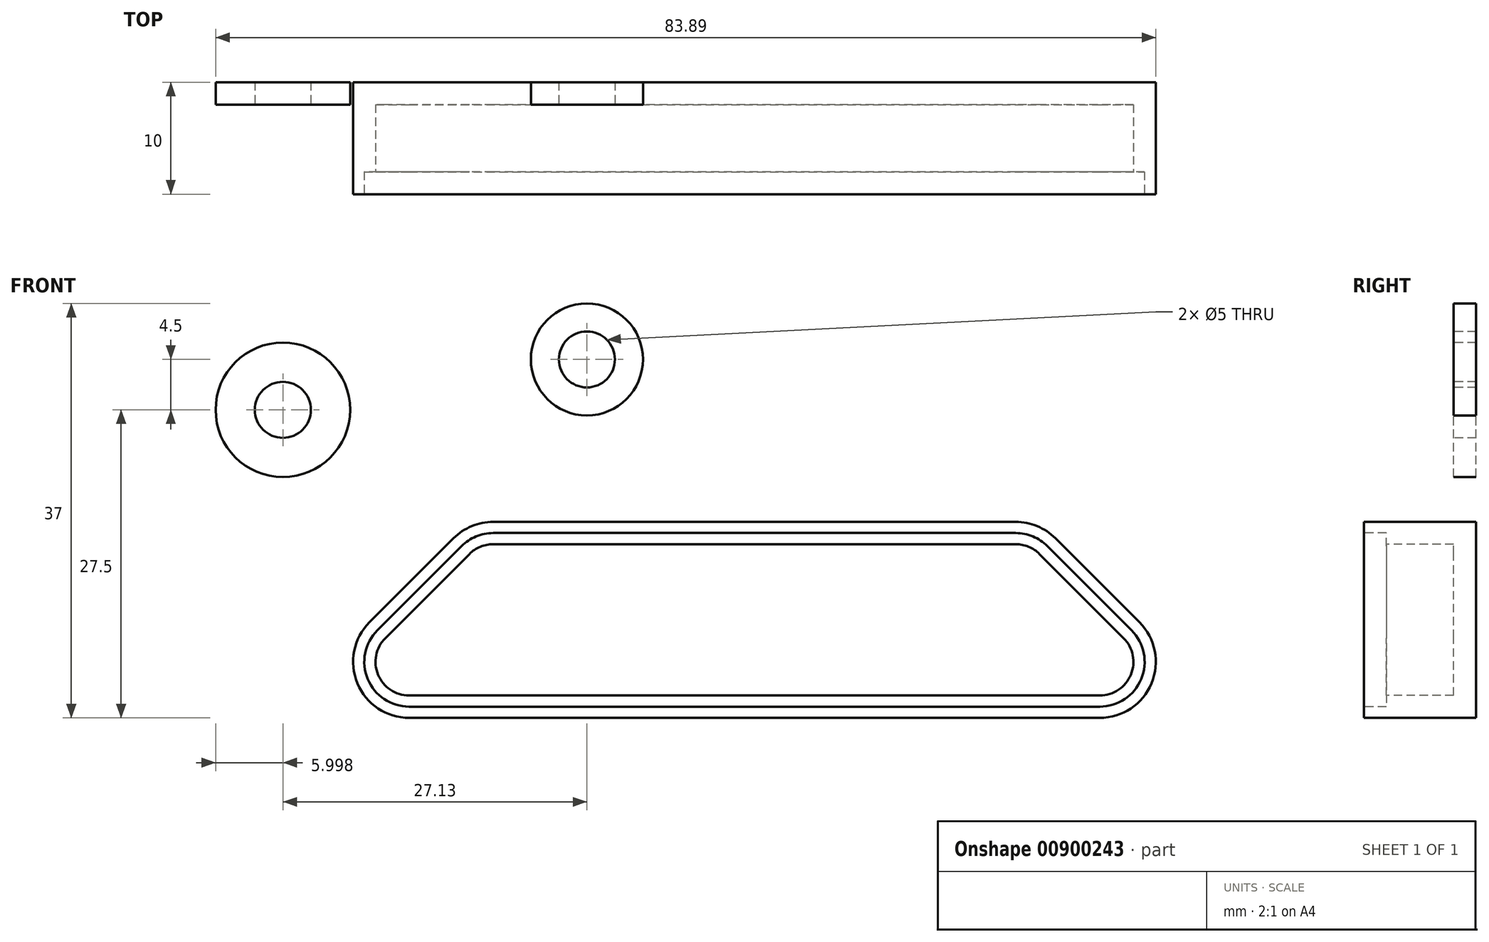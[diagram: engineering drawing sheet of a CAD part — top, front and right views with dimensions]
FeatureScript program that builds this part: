
annotation { "Feature Type Name" : "Feature", "Feature Type Description" : "" }
export const myFeature = defineFeature(function(context is Context, id is Id, definition is map)
    precondition{}
    {
        {
            var Q0;
            Q0=qCreatedBy(makeId("Front.planeOp"),FACE);
            var sketch = newSketch(context, id + "F0", { "sketchPlane" : qUnion([Q0])});
            skLineSegment(sketch, "E0", {"start": v(-37.2, 0) * mm, "end": v(34.97, 0) * mm, "construction": true});
            skArc(sketch, "E1", {"start": v(34.97, -20) * mm, "mid": v(54.97, 0) * mm, "end": v(34.97, 20) * mm});
            skArc(sketch, "E2", {"start": v(-37.2, 20) * mm, "mid": v(-57.2, 0) * mm, "end": v(-37.2, -20) * mm});
            skLineSegment(sketch, "E3", {"start": v(-37.2, 20) * mm, "end": v(34.97, 20) * mm});
            skLineSegment(sketch, "E4.MirrorCS", {"start": v(-37.2, -20) * mm, "end": v(34.97, -20) * mm});
            skSolve(sketch);
        }
        {
            var Q0;
            Q0=qSketchRegion(id+"F0",true);
            extrude(context, id + "F1", {"entities" : qUnion([Q0]), "depth" : 2 * mm, "offsetDistance" : 25 * mm});
        }
        {
            var Q0;
            Q0=makeQuery(id+"F1.opExtrude","CAP_FACE",FACE,{"disambiguationData":[OSD([sQuery(id+"F0.wireOp",EDGE,"E1"),sQuery(id+"F0.wireOp",EDGE,"E2"),sQuery(id+"F0.wireOp",EDGE,"E3"),sQuery(id+"F0.wireOp",EDGE,"E4.MirrorCS")])],"isStart":false});
            var sketch = newSketch(context, id + "F2", { "sketchPlane" : qUnion([Q0])});
            skLineSegment(sketch, "E5", {"start": v(0, 107.5) * mm, "end": v(0, -106.96) * mm, "construction": true});
            skLineSegment(sketch, "E6", {"start": v(0, -2.5) * mm, "end": v(23.31, -2.5) * mm});
            skLineSegment(sketch, "E7", {"start": v(26.85, -3.96) * mm, "end": v(34.35, -11.46) * mm});
            skLineSegment(sketch, "E8", {"start": v(30.81, -20) * mm, "end": v(0, -20) * mm});
            skArc(sketch, "E9.filletArc", {"start": v(26.85, -3.96) * mm, "mid": v(25.23, -2.88) * mm, "end": v(23.31, -2.5) * mm});
            skArc(sketch, "E10.filletArc", {"start": v(30.81, -20) * mm, "mid": v(35.43, -16.91) * mm, "end": v(34.35, -11.46) * mm});
            skLineSegment(sketch, "E11.MirrorCS", {"start": v(0, -2.5) * mm, "end": v(-23.31, -2.5) * mm});
            skArc(sketch, "E12.MirrorCS", {"start": v(-26.85, -3.96) * mm, "mid": v(-25.23, -2.88) * mm, "end": v(-23.31, -2.5) * mm});
            skLineSegment(sketch, "E13.MirrorCS", {"start": v(-26.85, -3.96) * mm, "end": v(-34.35, -11.46) * mm});
            skArc(sketch, "E14.MirrorCS", {"start": v(-30.81, -20) * mm, "mid": v(-35.43, -16.91) * mm, "end": v(-34.35, -11.46) * mm});
            skLineSegment(sketch, "E15.MirrorCS", {"start": v(-30.81, -20) * mm, "end": v(0, -20) * mm});
            skSolve(sketch);
        }
        {
            var Q0;
            Q0=makeQuery(id+"F2.imprint","IMPRINT",FACE,{"disambiguationData":[TD([[makeQuery(id+"F2.imprint","IMPRINT",EDGE,{"derivedFrom":sQuery(id+"F2.wireOp",EDGE,"E6")}),-1.0]])]});
            var Q1;
            Q1=makeQuery(id+"F2.imprint","IMPRINT",FACE,{"disambiguationData":[TD([[makeQuery(id+"F2.imprint","IMPRINT",EDGE,{"derivedFrom":sQuery(id+"F2.wireOp",EDGE,"1ff64fa8-2fd5-4123-b6a7-406101e30ad4.0")}),1.0]])]});
            var Q2;
            Q2=makeQuery(id+"F2.imprint","IMPRINT",FACE,{"disambiguationData":[TD([[makeQuery(id+"F2.imprint","IMPRINT",EDGE,{"derivedFrom":sQuery(id+"F2.wireOp",EDGE,"6d2cac0a-8418-49f5-aced-8188614ca164.0")}),1.0]])]});
            extrude(context, id + "F3", {"entities" : qUnion([Q0, Q1, Q2]), "operationType" : NewBodyOperationType.ADD, "depth" : 8 * mm, "offsetDistance" : 25 * mm});
        }
        {
            var Q0;
            Q0=makeQuery(id+"F3.opExtrude","CAP_FACE",FACE,{"disambiguationData":[OSD([sQuery(id+"F2.wireOp",EDGE,"E6"),sQuery(id+"F2.wireOp",EDGE,"E7"),sQuery(id+"F2.wireOp",EDGE,"E8"),sQuery(id+"F2.wireOp",EDGE,"E9.filletArc"),sQuery(id+"F2.wireOp",EDGE,"E10.filletArc"),sQuery(id+"F2.wireOp",EDGE,"E11.MirrorCS"),sQuery(id+"F2.wireOp",EDGE,"E12.MirrorCS"),sQuery(id+"F2.wireOp",EDGE,"E13.MirrorCS"),sQuery(id+"F2.wireOp",EDGE,"E14.MirrorCS"),sQuery(id+"F2.wireOp",EDGE,"E15.MirrorCS")])],"isStart":false});
            var sketch = newSketch(context, id + "F4", { "sketchPlane" : qUnion([Q0])});
            skArc(sketch, "E16.0", {"start": v(-33.64, -12.17) * mm, "mid": v(-34.51, -16.53) * mm, "end": v(-30.81, -19) * mm});
            skLineSegment(sketch, "E16.1", {"start": v(-26.14, -4.67) * mm, "end": v(-33.64, -12.17) * mm});
            skLineSegment(sketch, "E16.2", {"start": v(-30.81, -19) * mm, "end": v(30.81, -19) * mm});
            skArc(sketch, "E16.3", {"start": v(-23.31, -3.5) * mm, "mid": v(-24.85, -3.8) * mm, "end": v(-26.14, -4.67) * mm});
            skArc(sketch, "E16.4", {"start": v(30.81, -19) * mm, "mid": v(34.51, -16.53) * mm, "end": v(33.64, -12.17) * mm});
            skLineSegment(sketch, "E16.5", {"start": v(33.64, -12.17) * mm, "end": v(26.14, -4.67) * mm});
            skArc(sketch, "E16.6", {"start": v(26.14, -4.67) * mm, "mid": v(24.85, -3.8) * mm, "end": v(23.31, -3.5) * mm});
            skLineSegment(sketch, "E16.7", {"start": v(23.31, -3.5) * mm, "end": v(-23.31, -3.5) * mm});
            skSolve(sketch);
        }
        {
            var Q0;
            Q0=makeQuery(id+"F4.imprint","IMPRINT",FACE,{"disambiguationData":[TD([[makeQuery(id+"F4.imprint","IMPRINT",EDGE,{"derivedFrom":sQuery(id+"F4.wireOp",EDGE,"E16.0")}),1.0]])]});
            extrude(context, id + "F5", {"entities" : qUnion([Q0]), "operationType" : NewBodyOperationType.REMOVE, "oppositeDirection" : true, "depth" : 2 * mm, "offsetDistance" : 25 * mm});
        }
        {
            var Q0;
            Q0=makeQuery(id+"F5.boolean.opBoolean","COPY",FACE,{"derivedFrom":makeQuery(id+"F5.opExtrude","CAP_FACE",FACE,{"disambiguationData":[OSD([sQuery(id+"F4.wireOp",EDGE,"E16.0"),sQuery(id+"F4.wireOp",EDGE,"E16.1"),sQuery(id+"F4.wireOp",EDGE,"E16.2"),sQuery(id+"F4.wireOp",EDGE,"E16.3"),sQuery(id+"F4.wireOp",EDGE,"E16.4"),sQuery(id+"F4.wireOp",EDGE,"E16.5"),sQuery(id+"F4.wireOp",EDGE,"E16.6"),sQuery(id+"F4.wireOp",EDGE,"E16.7")])],"isStart":false})});
            var sketch = newSketch(context, id + "F6", { "sketchPlane" : qUnion([Q0])});
            skLineSegment(sketch, "E17.0", {"start": v(32.94, -12.88) * mm, "end": v(25.44, -5.38) * mm});
            skArc(sketch, "E17.1", {"start": v(30.81, -18) * mm, "mid": v(33.59, -16.15) * mm, "end": v(32.94, -12.88) * mm});
            skArc(sketch, "E17.2", {"start": v(25.44, -5.38) * mm, "mid": v(24.46, -4.73) * mm, "end": v(23.31, -4.5) * mm});
            skLineSegment(sketch, "E17.3", {"start": v(-30.81, -18) * mm, "end": v(30.81, -18) * mm});
            skLineSegment(sketch, "E17.4", {"start": v(23.31, -4.5) * mm, "end": v(-23.31, -4.5) * mm});
            skArc(sketch, "E17.5", {"start": v(-23.31, -4.5) * mm, "mid": v(-24.46, -4.73) * mm, "end": v(-25.44, -5.38) * mm});
            skLineSegment(sketch, "E17.6", {"start": v(-25.44, -5.38) * mm, "end": v(-32.94, -12.88) * mm});
            skArc(sketch, "E17.7", {"start": v(-32.94, -12.88) * mm, "mid": v(-33.59, -16.15) * mm, "end": v(-30.81, -18) * mm});
            skSolve(sketch);
        }
        {
            var Q0;
            Q0=makeQuery(id+"F6.imprint","IMPRINT",FACE,{"disambiguationData":[TD([[makeQuery(id+"F6.imprint","IMPRINT",EDGE,{"derivedFrom":sQuery(id+"F6.wireOp",EDGE,"E17.0")}),1.0]])]});
            extrude(context, id + "F7", {"entities" : qUnion([Q0]), "operationType" : NewBodyOperationType.REMOVE, "oppositeDirection" : true, "depth" : 6 * mm, "offsetDistance" : 25 * mm});
        }
        {
            var Q0;
            Q0=makeQuery(id+"F1.opExtrude","CAP_FACE",FACE,{"disambiguationData":[OSD([sQuery(id+"F0.wireOp",EDGE,"E1"),sQuery(id+"F0.wireOp",EDGE,"E2"),sQuery(id+"F0.wireOp",EDGE,"E3"),sQuery(id+"F0.wireOp",EDGE,"E4.MirrorCS")])],"isStart":false});
            var sketch = newSketch(context, id + "F8", { "sketchPlane" : qUnion([Q0])});
            skCircle(sketch, "E18", {"center": v(42.08, 7.5) * mm, "radius": 6 * mm});
            skLineSegment(sketch, "E19", {"start": v(61.14, 0) * mm, "end": v(-61.86, 0) * mm, "construction": true});
            skLineSegment(sketch, "E20", {"start": v(0, 29.23) * mm, "end": v(0, -29.55) * mm, "construction": true});
            skCircle(sketch, "E21", {"center": v(14.95, 12) * mm, "radius": 5 * mm});
            skCircle(sketch, "E22.MirrorC", {"center": v(-42.08, 7.5) * mm, "radius": 6 * mm});
            skCircle(sketch, "E23.MirrorC", {"center": v(-14.95, 12) * mm, "radius": 5 * mm});
            skSolve(sketch);
        }
        {
            var Q0;
            Q0=makeQuery(id+"F8.imprint","IMPRINT",FACE,{"disambiguationData":[TD([[makeQuery(id+"F8.imprint","IMPRINT",EDGE,{"derivedFrom":sQuery(id+"F8.wireOp",EDGE,"E23.MirrorC")}),-1.0]])]});
            var Q1;
            Q1=makeQuery(id+"F8.imprint","IMPRINT",FACE,{"disambiguationData":[TD([[makeQuery(id+"F8.imprint","IMPRINT",EDGE,{"derivedFrom":sQuery(id+"F8.wireOp",EDGE,"E22.MirrorC")}),-1.0]])]});
            var Q2;
            Q2=makeQuery(id+"F8.imprint","IMPRINT",FACE,{"disambiguationData":[TD([[makeQuery(id+"F8.imprint","IMPRINT",EDGE,{"derivedFrom":sQuery(id+"F8.wireOp",EDGE,"E21")}),1.0]])]});
            var Q3;
            Q3=makeQuery(id+"F8.imprint","IMPRINT",FACE,{"disambiguationData":[TD([[makeQuery(id+"F8.imprint","IMPRINT",EDGE,{"derivedFrom":sQuery(id+"F8.wireOp",EDGE,"E18")}),1.0]])]});
            extrude(context, id + "F9", {"entities" : qUnion([Q0, Q1, Q2, Q3]), "operationType" : NewBodyOperationType.ADD, "depth" : 1 * mm, "offsetDistance" : 25 * mm});
        }
        {
            var Q0;
            Q0=makeQuery(id+"F9.opExtrude","CAP_FACE",FACE,{"disambiguationData":[OSD([sQuery(id+"F8.wireOp",EDGE,"E23.MirrorC")])],"isStart":false});
            var sketch = newSketch(context, id + "F10", { "sketchPlane" : qUnion([Q0])});
            skCircle(sketch, "E24", {"center": v(-14.95, 12) * mm, "radius": 2.5 * mm});
            skLineSegment(sketch, "E25", {"start": v(0, 25.65) * mm, "end": v(0, -22.35) * mm, "construction": true});
            skCircle(sketch, "E26.MirrorC", {"center": v(14.95, 12) * mm, "radius": 2.5 * mm});
            skSolve(sketch);
        }
        {
            var Q0;
            Q0=makeQuery(id+"F9.opExtrude","CAP_FACE",FACE,{"disambiguationData":[OSD([sQuery(id+"F8.wireOp",EDGE,"E22.MirrorC")])],"isStart":false});
            var sketch = newSketch(context, id + "F11", { "sketchPlane" : qUnion([Q0])});
            skCircle(sketch, "E27", {"center": v(-42.08, 7.5) * mm, "radius": 2.5 * mm});
            skLineSegment(sketch, "E28", {"start": v(0, 25.47) * mm, "end": v(0, -27.42) * mm, "construction": true});
            skCircle(sketch, "E29.MirrorC", {"center": v(42.08, 7.5) * mm, "radius": 2.5 * mm});
            skSolve(sketch);
        }
        {
            var Q0;
            Q0=makeQuery(id+"F10.imprint","IMPRINT",FACE,{"disambiguationData":[TD([[makeQuery(id+"F10.imprint","IMPRINT",EDGE,{"derivedFrom":sQuery(id+"F10.wireOp",EDGE,"E24")}),1.0]])]});
            var Q1;
            Q1=makeQuery(id+"F11.imprint","IMPRINT",FACE,{"disambiguationData":[TD([[makeQuery(id+"F11.imprint","IMPRINT",EDGE,{"derivedFrom":sQuery(id+"F11.wireOp",EDGE,"E27")}),1.0]])]});
            var Q2;
            Q2=makeQuery(id+"F10.imprint","IMPRINT",FACE,{"disambiguationData":[TD([[makeQuery(id+"F10.imprint","IMPRINT",EDGE,{"derivedFrom":sQuery(id+"F10.wireOp",EDGE,"E26.MirrorC")}),-1.0]])]});
            var Q3;
            Q3=makeQuery(id+"F11.imprint","IMPRINT",FACE,{"disambiguationData":[TD([[makeQuery(id+"F11.imprint","IMPRINT",EDGE,{"derivedFrom":sQuery(id+"F11.wireOp",EDGE,"E29.MirrorC")}),-1.0]])]});
            extrude(context, id + "F12", {"entities" : qUnion([Q0, Q1, Q2, Q3]), "operationType" : NewBodyOperationType.REMOVE, "endBound" : BoundingType.THROUGH_ALL, "oppositeDirection" : true, "depth" : 25 * mm, "offsetDistance" : 25 * mm});
        }
    });
